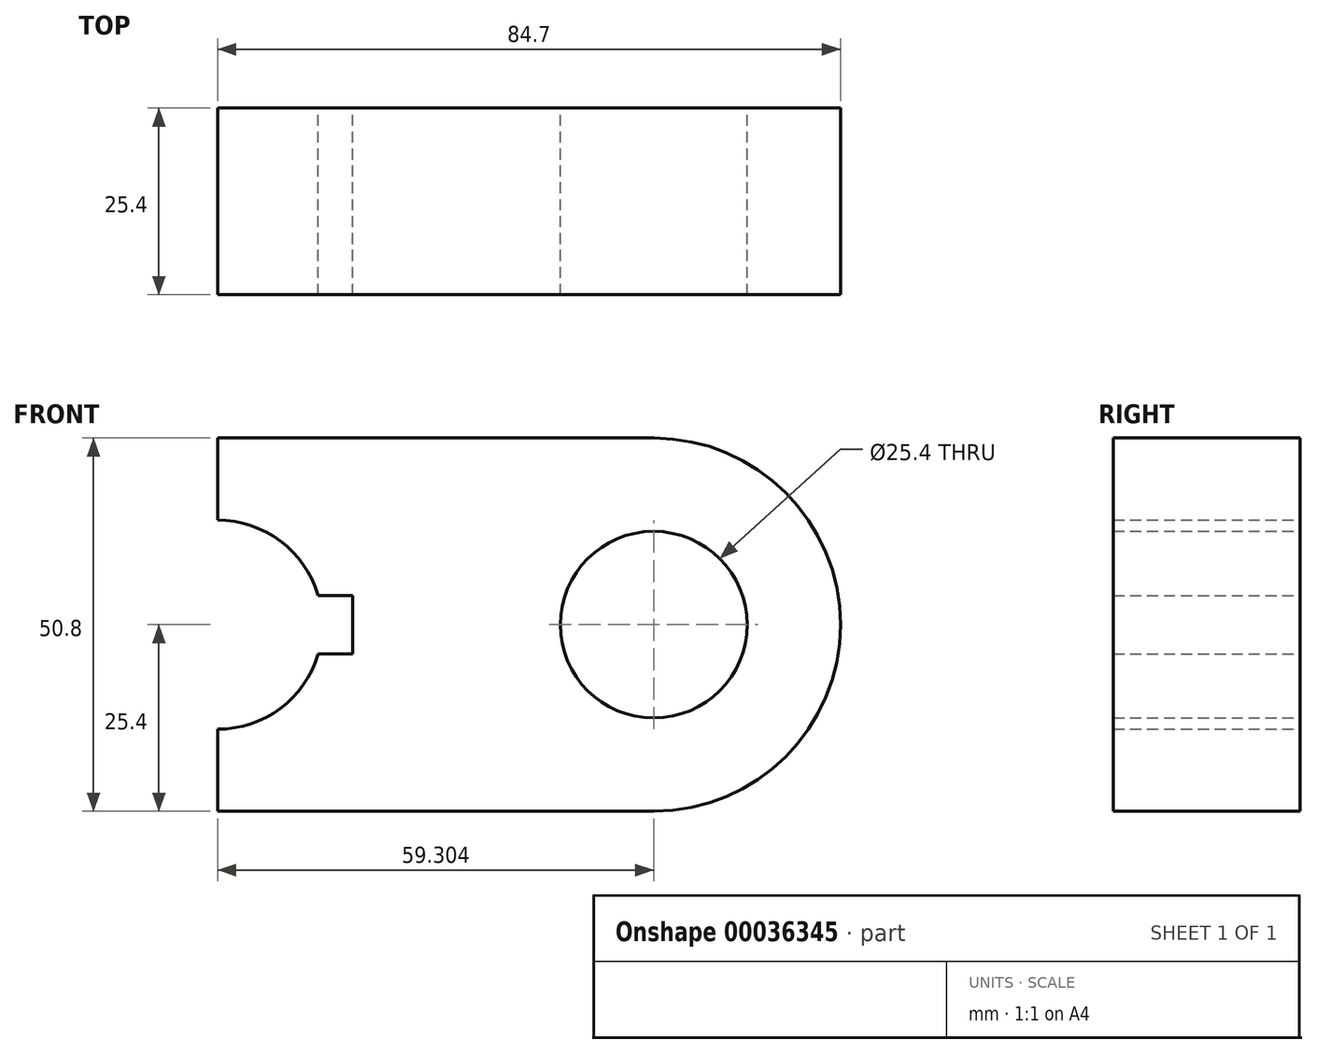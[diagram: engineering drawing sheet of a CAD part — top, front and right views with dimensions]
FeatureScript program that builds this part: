
annotation { "Feature Type Name" : "Feature", "Feature Type Description" : "" }
export const myFeature = defineFeature(function(context is Context, id is Id, definition is map)
    precondition{}
    {
        {
            var Q0;
            Q0=qCreatedBy(makeId("Front.planeOp"),FACE);
            var sketch = newSketch(context, id + "F0", { "sketchPlane" : qUnion([Q0])});
            skLineSegment(sketch, "E0.rect.bottom", {"start": v(-42.35, 25.4) * mm, "end": v(16.95, 25.4) * mm});
            skLineSegment(sketch, "E0.rect.top", {"start": v(-42.35, -25.4) * mm, "end": v(16.95, -25.4) * mm});
            skLineSegment(sketch, "E0.rect.left", {"start": v(-42.35, 25.4) * mm, "end": v(-42.35, -25.4) * mm});
            skLineSegment(sketch, "E0.rect.right", {"start": v(42.35, 0) * mm, "end": v(42.35, 0) * mm});
            skPoint(sketch, "E0.rect.middle", {"position": v(0, 0) * mm});
            skCircle(sketch, "E1", {"center": v(-42.35, 0) * mm, "radius": 25.4 * mm});
            skCircle(sketch, "E2", {"center": v(-42.35, 0) * mm, "radius": 14.22 * mm});
            skLineSegment(sketch, "E3.rect.bottom", {"start": v(-24, -4) * mm, "end": v(-32.27, -4) * mm});
            skLineSegment(sketch, "E3.rect.top", {"start": v(-24, 4) * mm, "end": v(-32.27, 4) * mm});
            skLineSegment(sketch, "E3.rect.left", {"start": v(-24, -4) * mm, "end": v(-24, 4) * mm});
            skLineSegment(sketch, "E3.rect.right", {"start": v(-32.27, -4) * mm, "end": v(-32.27, 4) * mm});
            skPoint(sketch, "E3.rect.middle", {"position": v(-28.13, 0) * mm});
            skPoint(sketch, "E4.centerSnap0", {"position": v(42.35, 0) * mm});
            skPoint(sketch, "E5.visualSharp", {"position": v(42.35, 25.4) * mm});
            skArc(sketch, "E5.filletArc", {"start": v(42.35, 0) * mm, "mid": v(34.91, 17.96) * mm, "end": v(16.95, 25.4) * mm});
            skPoint(sketch, "E6.visualSharp", {"position": v(42.35, -25.4) * mm});
            skArc(sketch, "E6.filletArc", {"start": v(16.95, -25.4) * mm, "mid": v(34.91, -17.96) * mm, "end": v(42.35, 0) * mm});
            skCircle(sketch, "E7", {"center": v(16.95, 0) * mm, "radius": 12.7 * mm});
            skLineSegment(sketch, "E8", {"start": v(-28.7, 4) * mm, "end": v(-28.7, -4) * mm});
            skSolve(sketch);
        }
        {
            var Q0;
            {var subQ3=sQuery(id+"F0.wireOp",EDGE,"E0.rect.bottom");Q0=makeQuery(id+"F0.imprint","IMPRINT",FACE,{"disambiguationData":[TD([[makeQuery(id+"F0.imprint","IMPRINT",EDGE,{"derivedFrom":subQ3}),-1.0]])]});}
            var Q1;
            {var subQ0=sQuery(id+"F0.wireOp",EDGE,"E2");var subQ1=sQuery(id+"F0.wireOp",EDGE,"E0.rect.left");var subQ3=makeQuery(id+"F0.imprint","INTERSECT",VERTEX,{"disambiguationData":[OD(0.0)],"derivedFrom":[subQ1,subQ0]});Q1=makeQuery(id+"F0.imprint","IMPRINT",FACE,{"disambiguationData":[TD([[makeQuery(id+"F0.imprint","IMPRINT",EDGE,{"disambiguationData":[TD([[subQ3,-1.0]])],"derivedFrom":subQ0}),-1.0]])]});}
            var Q2;
            {var subQ0=sQuery(id+"F0.wireOp",EDGE,"E3.rect.left");Q2=makeQuery(id+"F0.imprint","IMPRINT",FACE,{"disambiguationData":[TD([[makeQuery(id+"F0.imprint","IMPRINT",EDGE,{"derivedFrom":subQ0}),-1.0]])]});}
            extrude(context, id + "F1", {"entities" : qUnion([Q0, Q1, Q2]), "depth" : 25.4 * mm});
        }
    });
